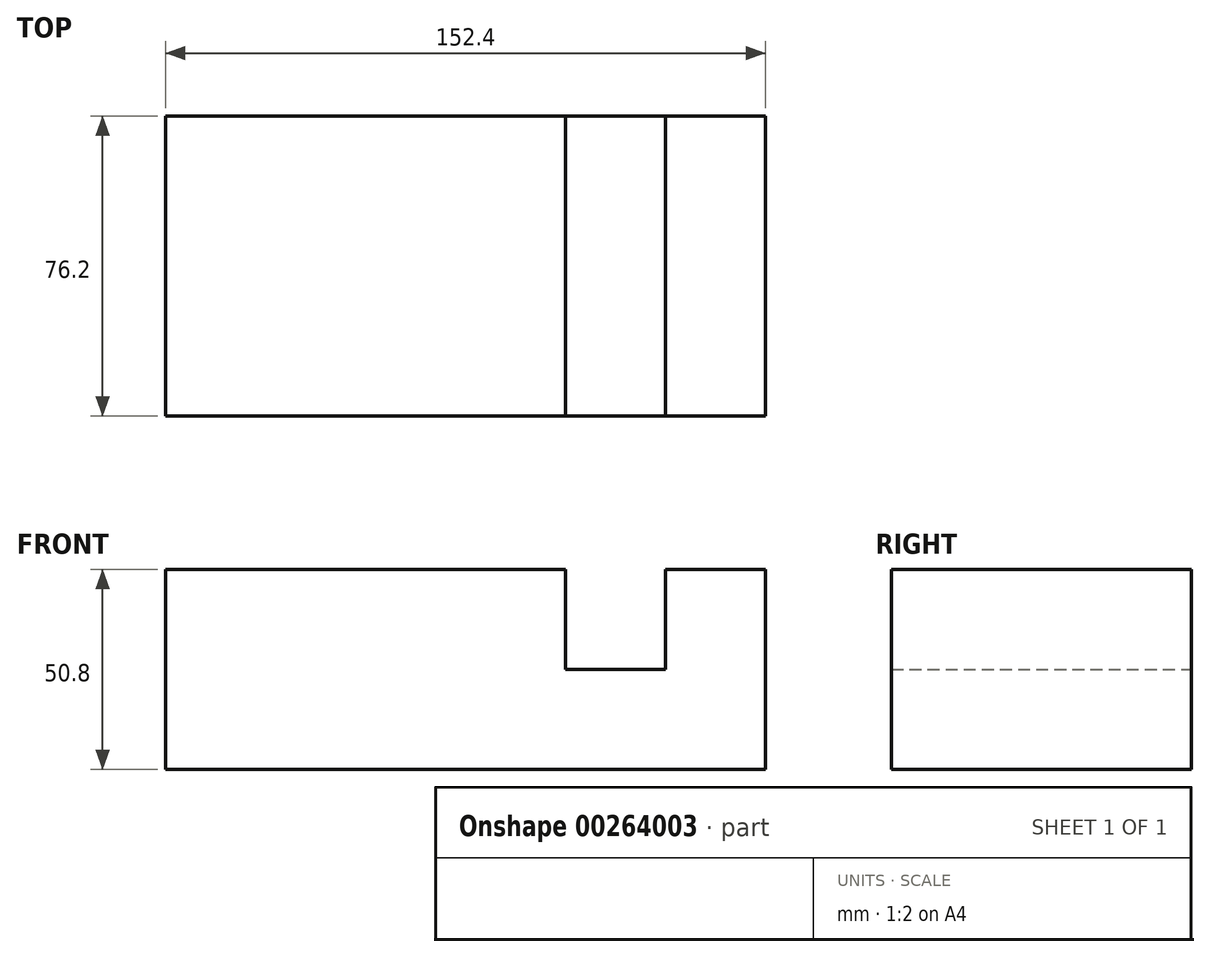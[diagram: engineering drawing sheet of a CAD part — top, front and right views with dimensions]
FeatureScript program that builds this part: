
annotation { "Feature Type Name" : "Feature", "Feature Type Description" : "" }
export const myFeature = defineFeature(function(context is Context, id is Id, definition is map)
    precondition{}
    {
        {
            var Q0;
            Q0=qCreatedBy(makeId("Front.planeOp"),FACE);
            var sketch = newSketch(context, id + "F0", { "sketchPlane" : qUnion([Q0])});
            skLineSegment(sketch, "E0", {"start": v(-75.4, 0) * mm, "end": v(77, 0) * mm});
            skLineSegment(sketch, "E1", {"start": v(-75.4, 0) * mm, "end": v(-75.4, 50.8) * mm});
            skLineSegment(sketch, "E2", {"start": v(-75.4, 50.8) * mm, "end": v(26.2, 50.8) * mm});
            skLineSegment(sketch, "E3", {"start": v(77, 0) * mm, "end": v(77, 50.8) * mm});
            skLineSegment(sketch, "E4", {"start": v(26.2, 50.8) * mm, "end": v(26.2, 25.4) * mm});
            skLineSegment(sketch, "E5", {"start": v(77, 50.8) * mm, "end": v(51.6, 50.8) * mm});
            skLineSegment(sketch, "E6", {"start": v(26.2, 25.4) * mm, "end": v(51.6, 25.4) * mm});
            skLineSegment(sketch, "E7", {"start": v(51.6, 50.8) * mm, "end": v(51.6, 25.4) * mm});
            skSolve(sketch);
        }
        {
            var Q0;
            Q0 = qSketchRegion(id + "F0", true);
            extrude(context, id + "F1", {"entities" : qUnion([Q0]), "depth" : 76.2 * mm});
        }
    });
